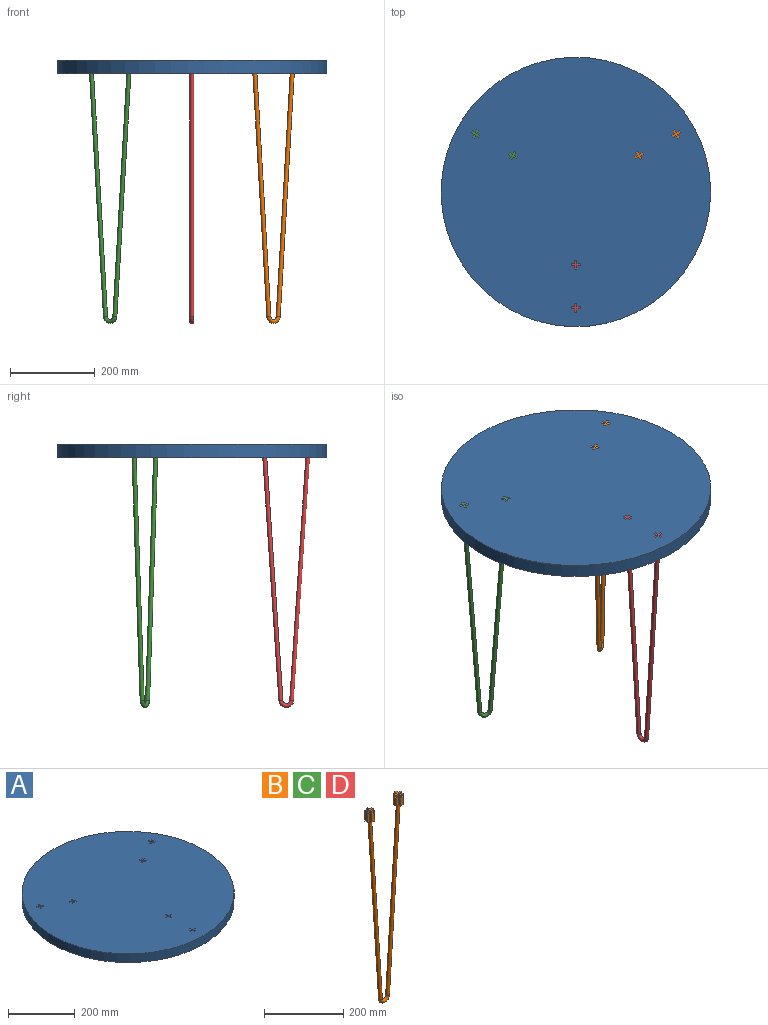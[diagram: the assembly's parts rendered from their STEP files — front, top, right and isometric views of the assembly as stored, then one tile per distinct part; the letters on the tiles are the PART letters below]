
ASSEMBLY  parts=4 mates=3
PART A: 153 faces, bbox 635x635x31.8 mm
  f0: plane 27.08x27.08mm, normal (0,0,-1), area 232.3mm2, adj f7,f8,f9,f10,f11,f12,f13,f14
  f1: plane 27.08x27.08mm, normal (0,0,-1), area 232.3mm2, adj f32,f33,f34,f35,f36,f37,f38,f39
  f2: plane 25.4x25.4mm, normal (0,0,-1), area 232.3mm2, adj f44,f45,f46,f47,f48,f49,f50,f51
  f3: plane 25.4x25.4mm, normal (0,0,-1), area 232.3mm2, adj f69,f70,f71,f72,f73,f74,f75,f76
  f4: plane 635x635mm, normal (0,0,1), area 315608.3mm2, adj f6,f81,f82,f83,f84,f85,f86,f87
  f5: plane 635x635mm, normal (0,0,-1), area 314214.8mm2, adj f6,f7,f8,f9,f10,f11,f12,f13
  f6: cylinder r=317.5mm len=635mm, axis (0,0,-1), area 63338.4mm2, adj f4,f5
  f7: plane 19.05x6.6mm, normal (-0.5,0.87,0), area 145.2mm2, adj f0,f5,f8,f18
  f8: plane 19.05x6.6mm, normal (-0.87,-0.5,0), area 145.2mm2, adj f0,f5,f7,f9
  f9: plane 19.05x8.8mm, normal (-0.5,0.87,0), area 193.5mm2, adj f0,f5,f8,f10
  f10: plane 19.05x6.6mm, normal (0.87,0.5,0), area 145.2mm2, adj f0,f5,f9,f11
  f11: plane 19.05x6.6mm, normal (-0.5,0.87,0), area 145.2mm2, adj f0,f5,f10,f12
  f12: plane 19.05x8.8mm, normal (0.87,0.5,0), area 193.5mm2, adj f0,f5,f11,f13
  f13: plane 19.05x6.6mm, normal (0.5,-0.87,0), area 145.2mm2, adj f0,f5,f12,f14
  f14: plane 19.05x6.6mm, normal (0.87,0.5,0), area 145.2mm2, adj f0,f5,f13,f15
  f15: plane 19.05x8.8mm, normal (0.5,-0.87,0), area 193.5mm2, adj f0,f5,f14,f16
  f16: plane 19.05x6.6mm, normal (-0.87,-0.5,0), area 145.2mm2, adj f0,f5,f15,f17
  f17: plane 19.05x6.6mm, normal (0.5,-0.87,0), area 145.2mm2, adj f0,f5,f16,f18
  f18: plane 19.05x8.8mm, normal (-0.87,-0.5,0), area 193.5mm2, adj f0,f5,f7,f17
  f19: plane 19.05x8.8mm, normal (-0.5,-0.87,0), area 193.5mm2, adj f5,f20,f30,f31
  f20: plane 19.05x6.6mm, normal (-0.87,0.5,0), area 145.2mm2, adj f5,f19,f21,f31
  f21: plane 19.05x6.6mm, normal (-0.5,-0.87,0), area 145.2mm2, adj f5,f20,f22,f31
  f22: plane 19.05x8.8mm, normal (-0.87,0.5,0), area 193.5mm2, adj f5,f21,f23,f31
  f23: plane 19.05x6.6mm, normal (0.5,0.87,0), area 145.2mm2, adj f5,f22,f24,f31
  f24: plane 19.05x6.6mm, normal (-0.87,0.5,0), area 145.2mm2, adj f5,f23,f25,f31
  f25: plane 19.05x8.8mm, normal (0.5,0.87,0), area 193.5mm2, adj f5,f24,f26,f31
  f26: plane 19.05x6.6mm, normal (0.87,-0.5,0), area 145.2mm2, adj f5,f25,f27,f31
  f27: plane 19.05x6.6mm, normal (0.5,0.87,0), area 145.2mm2, adj f5,f26,f28,f31
  f28: plane 19.05x8.8mm, normal (0.87,-0.5,0), area 193.5mm2, adj f5,f27,f29,f31
  f29: plane 19.05x6.6mm, normal (-0.5,-0.87,0), area 145.2mm2, adj f5,f28,f30,f31
  f30: plane 19.05x6.6mm, normal (0.87,-0.5,0), area 145.2mm2, adj f5,f19,f29,f31
  f31: plane 27.08x27.08mm, normal (0,0,-1), area 232.3mm2, adj f19,f20,f21,f22,f23,f24,f25,f26
  f32: plane 19.05x6.6mm, normal (-0.5,-0.87,0), area 145.2mm2, adj f1,f5,f33,f43
  f33: plane 19.05x6.6mm, normal (0.87,-0.5,0), area 145.2mm2, adj f1,f5,f32,f34
  f34: plane 19.05x8.8mm, normal (-0.5,-0.87,0), area 193.5mm2, adj f1,f5,f33,f35
  f35: plane 19.05x6.6mm, normal (-0.87,0.5,0), area 145.2mm2, adj f1,f5,f34,f36
  f36: plane 19.05x6.6mm, normal (-0.5,-0.87,0), area 145.2mm2, adj f1,f5,f35,f37
  f37: plane 19.05x8.8mm, normal (-0.87,0.5,0), area 193.5mm2, adj f1,f5,f36,f38
  f38: plane 19.05x6.6mm, normal (0.5,0.87,0), area 145.2mm2, adj f1,f5,f37,f39
  f39: plane 19.05x6.6mm, normal (-0.87,0.5,0), area 145.2mm2, adj f1,f5,f38,f40
  f40: plane 19.05x8.8mm, normal (0.5,0.87,0), area 193.5mm2, adj f1,f5,f39,f41
  f41: plane 19.05x6.6mm, normal (0.87,-0.5,0), area 145.2mm2, adj f1,f5,f40,f42
  f42: plane 19.05x6.6mm, normal (0.5,0.87,0), area 145.2mm2, adj f1,f5,f41,f43
  f43: plane 19.05x8.8mm, normal (0.87,-0.5,0), area 193.5mm2, adj f1,f5,f32,f42
  f44: plane 19.05x7.62mm, normal (1,0,0), area 145.2mm2, adj f2,f5,f45,f55
  f45: plane 19.05x10.16mm, normal (0,-1,0), area 193.5mm2, adj f2,f5,f44,f46
  f46: plane 19.05x7.62mm, normal (-1,0,0), area 145.2mm2, adj f2,f5,f45,f47
  f47: plane 19.05x7.62mm, normal (0,-1,0), area 145.2mm2, adj f2,f5,f46,f48
  f48: plane 19.05x10.16mm, normal (-1,0,0), area 193.5mm2, adj f2,f5,f47,f49
  f49: plane 19.05x7.62mm, normal (0,1,0), area 145.2mm2, adj f2,f5,f48,f50
  f50: plane 19.05x7.62mm, normal (-1,0,0), area 145.2mm2, adj f2,f5,f49,f51
  f51: plane 19.05x10.16mm, normal (0,1,0), area 193.5mm2, adj f2,f5,f50,f52
  f52: plane 19.05x7.62mm, normal (1,0,0), area 145.2mm2, adj f2,f5,f51,f53
  f53: plane 19.05x7.62mm, normal (0,1,0), area 145.2mm2, adj f2,f5,f52,f54
  f54: plane 19.05x10.16mm, normal (1,0,0), area 193.5mm2, adj f2,f5,f53,f55
  f55: plane 19.05x7.62mm, normal (0,-1,0), area 145.2mm2, adj f2,f5,f44,f54
  f56: plane 19.05x8.8mm, normal (-0.5,0.87,0), area 193.5mm2, adj f5,f57,f67,f68
  f57: plane 19.05x6.6mm, normal (0.87,0.5,0), area 145.2mm2, adj f5,f56,f58,f68
  f58: plane 19.05x6.6mm, normal (-0.5,0.87,0), area 145.2mm2, adj f5,f57,f59,f68
  f59: plane 19.05x8.8mm, normal (0.87,0.5,0), area 193.5mm2, adj f5,f58,f60,f68
  f60: plane 19.05x6.6mm, normal (0.5,-0.87,0), area 145.2mm2, adj f5,f59,f61,f68
  f61: plane 19.05x6.6mm, normal (0.87,0.5,0), area 145.2mm2, adj f5,f60,f62,f68
  f62: plane 19.05x8.8mm, normal (0.5,-0.87,0), area 193.5mm2, adj f5,f61,f63,f68
  f63: plane 19.05x6.6mm, normal (-0.87,-0.5,0), area 145.2mm2, adj f5,f62,f64,f68
  f64: plane 19.05x6.6mm, normal (0.5,-0.87,0), area 145.2mm2, adj f5,f63,f65,f68
  f65: plane 19.05x8.8mm, normal (-0.87,-0.5,0), area 193.5mm2, adj f5,f64,f66,f68
  f66: plane 19.05x6.6mm, normal (-0.5,0.87,0), area 145.2mm2, adj f5,f65,f67,f68
  f67: plane 19.05x6.6mm, normal (-0.87,-0.5,0), area 145.2mm2, adj f5,f56,f66,f68
  f68: plane 27.08x27.08mm, normal (0,0,-1), area 232.3mm2, adj f56,f57,f58,f59,f60,f61,f62,f63
  f69: plane 19.05x7.62mm, normal (-1,0,0), area 145.2mm2, adj f3,f5,f70,f80
  f70: plane 19.05x7.62mm, normal (0,-1,0), area 145.2mm2, adj f3,f5,f69,f71
  f71: plane 19.05x10.16mm, normal (-1,0,0), area 193.5mm2, adj f3,f5,f70,f72
  f72: plane 19.05x7.62mm, normal (0,1,0), area 145.2mm2, adj f3,f5,f71,f73
  f73: plane 19.05x7.62mm, normal (-1,0,0), area 145.2mm2, adj f3,f5,f72,f74
  f74: plane 19.05x10.16mm, normal (0,1,0), area 193.5mm2, adj f3,f5,f73,f75
  f75: plane 19.05x7.62mm, normal (1,0,0), area 145.2mm2, adj f3,f5,f74,f76
  f76: plane 19.05x7.62mm, normal (0,1,0), area 145.2mm2, adj f3,f5,f75,f77
  f77: plane 19.05x10.16mm, normal (1,0,0), area 193.5mm2, adj f3,f5,f76,f78
  f78: plane 19.05x7.62mm, normal (0,-1,0), area 145.2mm2, adj f3,f5,f77,f79
  f79: plane 19.05x7.62mm, normal (1,0,0), area 145.2mm2, adj f3,f5,f78,f80
  f80: plane 19.05x10.16mm, normal (0,-1,0), area 193.5mm2, adj f3,f5,f69,f79
  f81: plane 12.7x6.6mm, normal (-0.5,-0.87,0), area 96.8mm2, adj f1,f4,f82,f92
  f82: plane 12.7x6.6mm, normal (-0.87,0.5,0), area 96.8mm2, adj f1,f4,f81,f83
  f83: plane 12.7x4.4mm, normal (-0.5,-0.87,0), area 64.5mm2, adj f1,f4,f82,f84
  f84: plane 12.7x6.6mm, normal (0.87,-0.5,0), area 96.8mm2, adj f1,f4,f83,f85
  f85: plane 12.7x6.6mm, normal (-0.5,-0.87,0), area 96.8mm2, adj f1,f4,f84,f86
  f86: plane 12.7x4.4mm, normal (0.87,-0.5,0), area 64.5mm2, adj f1,f4,f85,f87
  f87: plane 12.7x6.6mm, normal (0.5,0.87,0), area 96.8mm2, adj f1,f4,f86,f88
  f88: plane 12.7x6.6mm, normal (0.87,-0.5,0), area 96.8mm2, adj f1,f4,f87,f89
  f89: plane 12.7x4.4mm, normal (0.5,0.87,0), area 64.5mm2, adj f1,f4,f88,f90
  f90: plane 12.7x6.6mm, normal (-0.87,0.5,0), area 96.8mm2, adj f1,f4,f89,f91
  f91: plane 12.7x6.6mm, normal (0.5,0.87,0), area 96.8mm2, adj f1,f4,f90,f92
  f92: plane 12.7x4.4mm, normal (-0.87,0.5,0), area 64.5mm2, adj f1,f4,f81,f91
  f93: plane 12.7x7.62mm, normal (0,-1,0), area 96.8mm2, adj f2,f4,f94,f104
  f94: plane 12.7x7.62mm, normal (-1,0,0), area 96.8mm2, adj f2,f4,f93,f95
  f95: plane 12.7x5.08mm, normal (0,-1,0), area 64.5mm2, adj f2,f4,f94,f96
  f96: plane 12.7x7.62mm, normal (1,0,0), area 96.8mm2, adj f2,f4,f95,f97
  f97: plane 12.7x7.62mm, normal (0,-1,0), area 96.8mm2, adj f2,f4,f96,f98
  f98: plane 12.7x5.08mm, normal (1,0,0), area 64.5mm2, adj f2,f4,f97,f99
  f99: plane 12.7x7.62mm, normal (0,1,0), area 96.8mm2, adj f2,f4,f98,f100
  f100: plane 12.7x7.62mm, normal (1,0,0), area 96.8mm2, adj f2,f4,f99,f101
  f101: plane 12.7x5.08mm, normal (0,1,0), area 64.5mm2, adj f2,f4,f100,f102
  f102: plane 12.7x7.62mm, normal (-1,0,0), area 96.8mm2, adj f2,f4,f101,f103
  f103: plane 12.7x7.62mm, normal (0,1,0), area 96.8mm2, adj f2,f4,f102,f104
  f104: plane 12.7x5.08mm, normal (-1,0,0), area 64.5mm2, adj f2,f4,f93,f103
  f105: plane 12.7x6.6mm, normal (-0.5,0.87,0), area 96.8mm2, adj f4,f68,f106,f116
  f106: plane 12.7x6.6mm, normal (0.87,0.5,0), area 96.8mm2, adj f4,f68,f105,f107
  f107: plane 12.7x4.4mm, normal (-0.5,0.87,0), area 64.5mm2, adj f4,f68,f106,f108
  f108: plane 12.7x6.6mm, normal (-0.87,-0.5,0), area 96.8mm2, adj f4,f68,f107,f109
  f109: plane 12.7x6.6mm, normal (-0.5,0.87,0), area 96.8mm2, adj f4,f68,f108,f110
  f110: plane 12.7x4.4mm, normal (-0.87,-0.5,0), area 64.5mm2, adj f4,f68,f109,f111
  f111: plane 12.7x6.6mm, normal (0.5,-0.87,0), area 96.8mm2, adj f4,f68,f110,f112
  f112: plane 12.7x6.6mm, normal (-0.87,-0.5,0), area 96.8mm2, adj f4,f68,f111,f113
  f113: plane 12.7x4.4mm, normal (0.5,-0.87,0), area 64.5mm2, adj f4,f68,f112,f114
  f114: plane 12.7x6.6mm, normal (0.87,0.5,0), area 96.8mm2, adj f4,f68,f113,f115
  f115: plane 12.7x6.6mm, normal (0.5,-0.87,0), area 96.8mm2, adj f4,f68,f114,f116
  f116: plane 12.7x4.4mm, normal (0.87,0.5,0), area 64.5mm2, adj f4,f68,f105,f115
  f117: plane 12.7x6.6mm, normal (-0.87,-0.5,0), area 96.8mm2, adj f0,f4,f118,f126
  f118: plane 12.7x4.4mm, normal (0.5,-0.87,0), area 64.5mm2, adj f0,f4,f117,f119
  f119: plane 12.7x6.6mm, normal (0.87,0.5,0), area 96.8mm2, adj f0,f4,f118,f120
  f120: plane 12.7x6.6mm, normal (0.5,-0.87,0), area 96.8mm2, adj f0,f4,f119,f121
  f121: plane 12.7x4.4mm, normal (0.87,0.5,0), area 64.5mm2, adj f0,f4,f120,f122
  f122: plane 12.7x6.6mm, normal (-0.5,0.87,0), area 96.8mm2, adj f0,f4,f121,f123
  f123: plane 12.7x6.6mm, normal (0.87,0.5,0), area 96.8mm2, adj f0,f4,f122,f124
  f124: plane 12.7x4.4mm, normal (-0.5,0.87,0), area 64.5mm2, adj f0,f4,f123,f125
  f125: plane 12.7x6.6mm, normal (-0.87,-0.5,0), area 96.8mm2, adj f0,f4,f124,f127
  f126: plane 12.7x6.6mm, normal (0.5,-0.87,0), area 96.8mm2, adj f0,f4,f117,f128
  f127: plane 12.7x6.6mm, normal (-0.5,0.87,0), area 96.8mm2, adj f0,f4,f125,f128
  f128: plane 12.7x4.4mm, normal (-0.87,-0.5,0), area 64.5mm2, adj f0,f4,f126,f127
  f129: plane 12.7x6.6mm, normal (-0.5,-0.87,0), area 96.8mm2, adj f4,f31,f130,f140
  f130: plane 12.7x6.6mm, normal (-0.87,0.5,0), area 96.8mm2, adj f4,f31,f129,f131
  f131: plane 12.7x4.4mm, normal (-0.5,-0.87,0), area 64.5mm2, adj f4,f31,f130,f132
  f132: plane 12.7x6.6mm, normal (0.87,-0.5,0), area 96.8mm2, adj f4,f31,f131,f133
  f133: plane 12.7x6.6mm, normal (-0.5,-0.87,0), area 96.8mm2, adj f4,f31,f132,f134
  f134: plane 12.7x4.4mm, normal (0.87,-0.5,0), area 64.5mm2, adj f4,f31,f133,f135
  f135: plane 12.7x6.6mm, normal (0.5,0.87,0), area 96.8mm2, adj f4,f31,f134,f136
  f136: plane 12.7x6.6mm, normal (0.87,-0.5,0), area 96.8mm2, adj f4,f31,f135,f137
  f137: plane 12.7x4.4mm, normal (0.5,0.87,0), area 64.5mm2, adj f4,f31,f136,f138
  f138: plane 12.7x6.6mm, normal (-0.87,0.5,0), area 96.8mm2, adj f4,f31,f137,f139
  f139: plane 12.7x6.6mm, normal (0.5,0.87,0), area 96.8mm2, adj f4,f31,f138,f140
  f140: plane 12.7x4.4mm, normal (-0.87,0.5,0), area 64.5mm2, adj f4,f31,f129,f139
  f141: plane 12.7x7.62mm, normal (1,0,0), area 96.8mm2, adj f3,f4,f142,f152
  f142: plane 12.7x7.62mm, normal (0,-1,0), area 96.8mm2, adj f3,f4,f141,f143
  f143: plane 12.7x5.08mm, normal (1,0,0), area 64.5mm2, adj f3,f4,f142,f144
  f144: plane 12.7x7.62mm, normal (0,1,0), area 96.8mm2, adj f3,f4,f143,f145
  f145: plane 12.7x7.62mm, normal (1,0,0), area 96.8mm2, adj f3,f4,f144,f146
  f146: plane 12.7x5.08mm, normal (0,1,0), area 64.5mm2, adj f3,f4,f145,f147
  f147: plane 12.7x7.62mm, normal (-1,0,0), area 96.8mm2, adj f3,f4,f146,f148
  f148: plane 12.7x7.62mm, normal (0,1,0), area 96.8mm2, adj f3,f4,f147,f149
  f149: plane 12.7x5.08mm, normal (-1,0,0), area 64.5mm2, adj f3,f4,f148,f150
  f150: plane 12.7x7.62mm, normal (0,-1,0), area 96.8mm2, adj f3,f4,f149,f151
  f151: plane 12.7x7.62mm, normal (-1,0,0), area 96.8mm2, adj f3,f4,f150,f152
  f152: plane 12.7x5.08mm, normal (0,-1,0), area 64.5mm2, adj f3,f4,f141,f151
PART B: 59 faces, bbox 128.4x26.8x621.1 mm
  f0: plane 25.4x25.4mm, normal (0,0,1), area 232.3mm2, adj f20,f21,f22,f23,f24,f25,f26,f27
  f1: plane 25.4x25.4mm, normal (0,0,1), area 232.3mm2, adj f7,f8,f9,f10,f11,f12,f13,f14
  f2: plane 10.87x6.11mm, normal (0.13,0,0.99), area 35.6mm2, adj f3,f5
  f3: bspline ~34.73x16.66mm, area 1140.6mm2, adj f2,f4,f6
  f4: bspline ~571.92x47.65mm, area 17166.1mm2, adj f3,f19
  f5: plane 10.88x6.15mm, normal (0,0,-1), area 35.6mm2, adj f2,f6
  f6: bspline ~577.64x48.03mm, area 17166.1mm2, adj f3,f5,f32
  f7: plane 25.4x7.62mm, normal (-1,0,0), area 193.5mm2, adj f1,f8,f18,f19
  f8: plane 25.4x7.62mm, normal (0,1,0), area 193.5mm2, adj f1,f7,f9,f19
  f9: plane 25.4x10.16mm, normal (-1,0,0), area 258.1mm2, adj f1,f8,f10,f19
  f10: plane 25.4x7.62mm, normal (0,-1,0), area 193.5mm2, adj f1,f9,f11,f19
  f11: plane 25.4x7.62mm, normal (-1,0,0), area 193.5mm2, adj f1,f10,f12,f19
  f12: plane 25.4x10.16mm, normal (0,-1,0), area 258.1mm2, adj f1,f11,f13,f19
  f13: plane 25.4x7.62mm, normal (1,0,0), area 193.5mm2, adj f1,f12,f14,f19
  f14: plane 25.4x7.62mm, normal (0,-1,0), area 193.5mm2, adj f1,f13,f15,f19
  f15: plane 25.4x10.16mm, normal (1,0,0), area 258.1mm2, adj f1,f14,f16,f19
  f16: plane 25.4x7.62mm, normal (0,1,0), area 193.5mm2, adj f1,f15,f17,f19
  f17: plane 25.4x7.62mm, normal (1,0,0), area 193.5mm2, adj f1,f16,f18,f19
  f18: plane 25.4x10.16mm, normal (0,1,0), area 258.1mm2, adj f1,f7,f17,f19
  f19: plane 26.73x26.73mm, normal (0,0,-1), area 341.6mm2, adj f4,f7,f8,f9,f10,f11,f12,f13
  f20: plane 25.4x7.62mm, normal (1,0,0), area 193.5mm2, adj f0,f21,f31,f32
  f21: plane 25.4x7.62mm, normal (0,-1,0), area 193.5mm2, adj f0,f20,f22,f32
  f22: plane 25.4x10.16mm, normal (1,0,0), area 258.1mm2, adj f0,f21,f23,f32
  f23: plane 25.4x7.62mm, normal (0,1,0), area 193.5mm2, adj f0,f22,f24,f32
  f24: plane 25.4x7.62mm, normal (1,0,0), area 193.5mm2, adj f0,f23,f25,f32
  f25: plane 25.4x10.16mm, normal (0,1,0), area 258.1mm2, adj f0,f24,f26,f32
  f26: plane 25.4x7.62mm, normal (-1,0,0), area 193.5mm2, adj f0,f25,f27,f32
  f27: plane 25.4x7.62mm, normal (0,1,0), area 193.5mm2, adj f0,f26,f28,f32
  f28: plane 25.4x10.16mm, normal (-1,0,0), area 258.1mm2, adj f0,f27,f29,f32
  f29: plane 25.4x7.62mm, normal (0,-1,0), area 193.5mm2, adj f0,f28,f30,f32
  f30: plane 25.4x7.62mm, normal (-1,0,0), area 193.5mm2, adj f0,f29,f31,f32
  f31: plane 25.4x10.16mm, normal (0,-1,0), area 258.1mm2, adj f0,f20,f30,f32
  f32: plane 26.73x26.73mm, normal (0,0,-1), area 341.6mm2, adj f6,f20,f21,f22,f23,f24,f25,f26
  f33: plane 6.35x5.08mm, normal (0,-1,0), area 32.3mm2, adj f1,f34,f44,f45
  f34: plane 7.62x6.35mm, normal (1,0,0), area 48.4mm2, adj f1,f33,f35,f45
  f35: plane 7.62x6.35mm, normal (0,-1,0), area 48.4mm2, adj f1,f34,f36,f45
  f36: plane 6.35x5.08mm, normal (1,0,0), area 32.3mm2, adj f1,f35,f37,f45
  f37: plane 7.62x6.35mm, normal (0,1,0), area 48.4mm2, adj f1,f36,f38,f45
  f38: plane 7.62x6.35mm, normal (1,0,0), area 48.4mm2, adj f1,f37,f39,f45
  f39: plane 6.35x5.08mm, normal (0,1,0), area 32.3mm2, adj f1,f38,f40,f45
  f40: plane 7.62x6.35mm, normal (-1,0,0), area 48.4mm2, adj f1,f39,f41,f45
  f41: plane 7.62x6.35mm, normal (0,1,0), area 48.4mm2, adj f1,f40,f42,f45
  f42: plane 6.35x5.08mm, normal (-1,0,0), area 32.3mm2, adj f1,f41,f43,f45
  f43: plane 7.62x6.35mm, normal (0,-1,0), area 48.4mm2, adj f1,f42,f44,f45
  f44: plane 7.62x6.35mm, normal (-1,0,0), area 48.4mm2, adj f1,f33,f43,f45
  f45: plane 20.32x20.32mm, normal (0,0,1), area 180.6mm2, adj f33,f34,f35,f36,f37,f38,f39,f40
  f46: plane 6.35x5.08mm, normal (0,-1,0), area 32.3mm2, adj f0,f47,f57,f58
  f47: plane 7.62x6.35mm, normal (1,0,0), area 48.4mm2, adj f0,f46,f48,f58
  f48: plane 7.62x6.35mm, normal (0,-1,0), area 48.4mm2, adj f0,f47,f49,f58
  f49: plane 6.35x5.08mm, normal (1,0,0), area 32.3mm2, adj f0,f48,f50,f58
  f50: plane 7.62x6.35mm, normal (0,1,0), area 48.4mm2, adj f0,f49,f51,f58
  f51: plane 7.62x6.35mm, normal (1,0,0), area 48.4mm2, adj f0,f50,f52,f58
  f52: plane 6.35x5.08mm, normal (0,1,0), area 32.3mm2, adj f0,f51,f53,f58
  f53: plane 7.62x6.35mm, normal (-1,0,0), area 48.4mm2, adj f0,f52,f54,f58
  f54: plane 7.62x6.35mm, normal (0,1,0), area 48.4mm2, adj f0,f53,f55,f58
  f55: plane 6.35x5.08mm, normal (-1,0,0), area 32.3mm2, adj f0,f54,f56,f58
  f56: plane 7.62x6.35mm, normal (0,-1,0), area 48.4mm2, adj f0,f55,f57,f58
  f57: plane 7.62x6.35mm, normal (-1,0,0), area 48.4mm2, adj f0,f46,f56,f58
  f58: plane 20.32x20.32mm, normal (0,0,1), area 180.6mm2, adj f46,f47,f48,f49,f50,f51,f52,f53
PART C: same geometry as B
PART D: same geometry as B
PLACE A t=(0,0,-31.75)mm
PLACE B rot(axis=(0,0,1),30deg) t=(236.47,136.52,-31.75)mm
PLACE C rot(axis=(0,0,-1),30deg) t=(-148.48,85.72,-31.75)mm
PLACE D rot(axis=(0,0,1),90deg) t=(0,-171.45,-31.75)mm
MATE revolute D.f45 <-> A.f4  axis (0,0,1) through (0,-273.05,0)mm
MATE revolute B.f58 <-> A.f4  axis (0,0,1) through (236.47,136.52,0)mm
MATE revolute C.f45 <-> A.f4  axis (0,0,1) through (-236.47,136.53,0)mm
